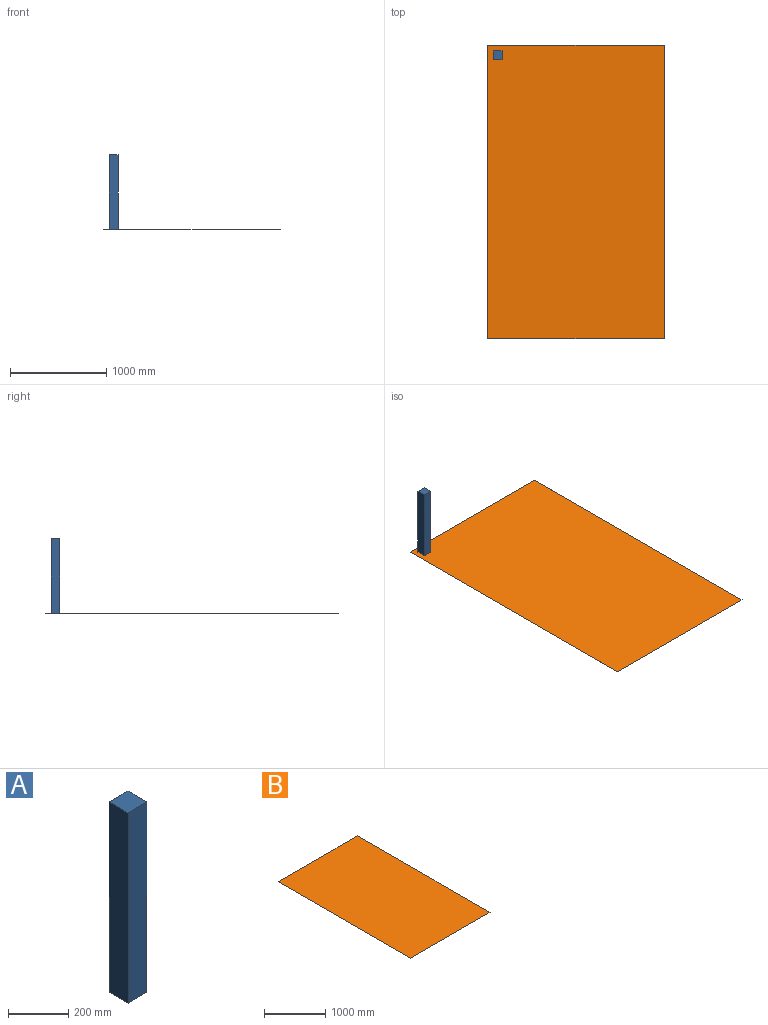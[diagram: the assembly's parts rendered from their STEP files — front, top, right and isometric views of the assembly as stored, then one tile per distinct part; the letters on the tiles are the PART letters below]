
ASSEMBLY  parts=2 mates=1
PART A: 6 faces, bbox 88.9x88.9x774.7 mm
  f0: plane 774.7x88.9mm, normal (1,0,0), area 68870.8mm2, adj f1,f3,f4,f5
  f1: plane 774.7x88.9mm, normal (0,1,0), area 68870.8mm2, adj f0,f2,f4,f5
  f2: plane 774.7x88.9mm, normal (-1,0,0), area 68870.8mm2, adj f1,f3,f4,f5
  f3: plane 774.7x88.9mm, normal (0,-1,0), area 68870.8mm2, adj f0,f2,f4,f5
  f4: plane 88.9x88.9mm, normal (0,0,-1), area 7903.2mm2, adj f0,f1,f2,f3
  f5: plane 88.9x88.9mm, normal (0,0,1), area 7903.2mm2, adj f0,f1,f2,f3
PART B: 6 faces, bbox 1828.8x3048x0 mm
  f0: plane 1828.8x0.03mm, normal (0,-1,0), area 46.5mm2, adj f1,f3,f4,f5
  f1: plane 3048x0.03mm, normal (1,0,0), area 77.4mm2, adj f0,f2,f4,f5
  f2: plane 1828.8x0.03mm, normal (0,1,0), area 46.5mm2, adj f1,f3,f4,f5
  f3: plane 3048x0.03mm, normal (-1,0,0), area 77.4mm2, adj f0,f2,f4,f5
  f4: plane 3048x1828.8mm, normal (0,0,1), area 5574182.4mm2, adj f0,f1,f2,f3
  f5: plane 3048x1828.8mm, normal (0,0,-1), area 5574182.4mm2, adj f0,f1,f2,f3
PLACE A t=(-812.91,1419.13,774.7)mm
PLACE B t=(0,0,-0.03)mm
MATE planar B.f4 <-> A.f4  axis (0,0,1) through (0,0,0)mm
